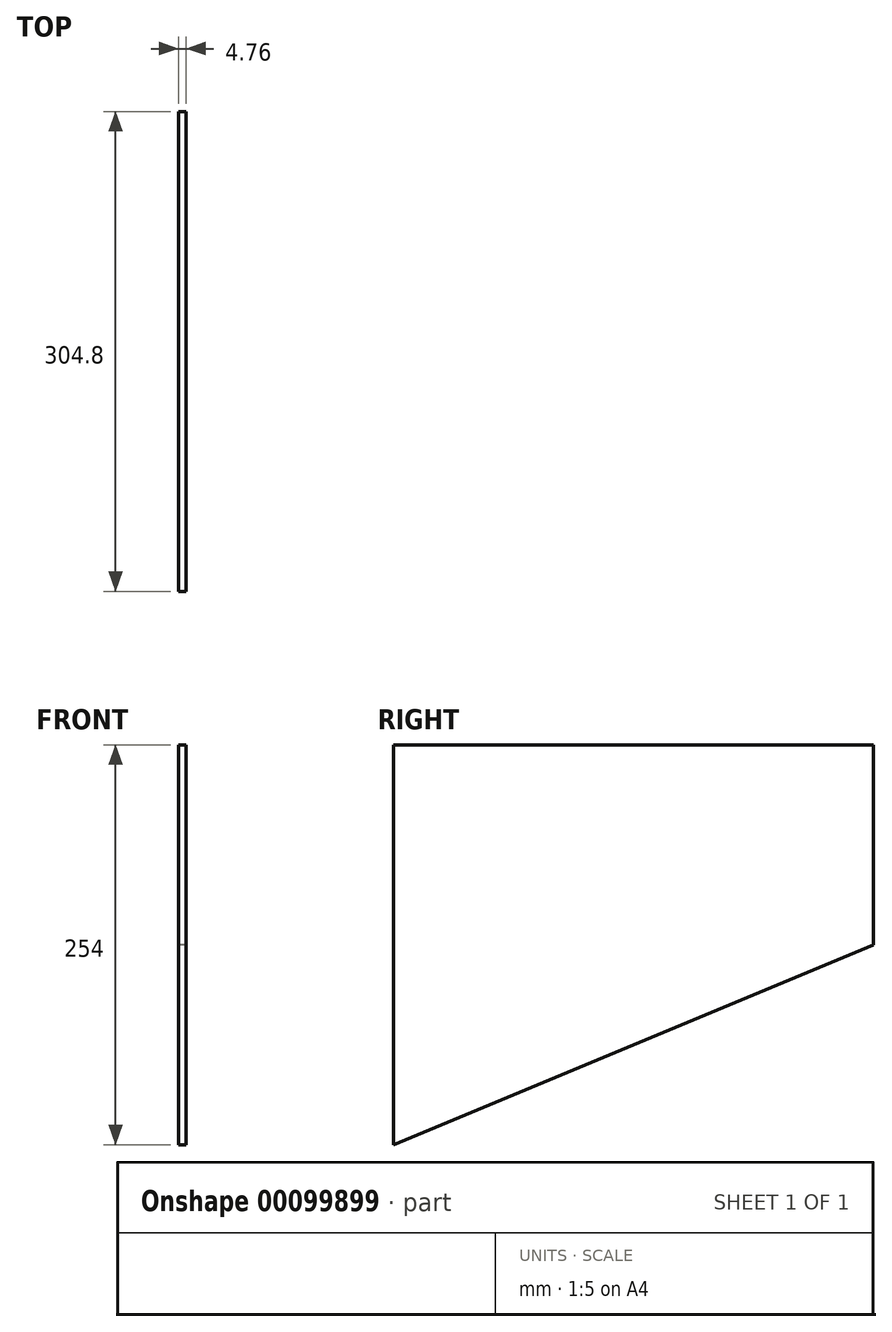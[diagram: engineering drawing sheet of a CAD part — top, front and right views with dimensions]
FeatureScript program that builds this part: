
annotation { "Feature Type Name" : "Feature", "Feature Type Description" : "" }
export const myFeature = defineFeature(function(context is Context, id is Id, definition is map)
    precondition{}
    {
        {
            var Q0;
            Q0=qCreatedBy(makeId("Right.planeOp"),FACE);
            var sketch = newSketch(context, id + "F0", { "sketchPlane" : qUnion([Q0])});
            skLineSegment(sketch, "E0", {"start": v(304.8, 19.22) * mm, "end": v(304.8, -107.78) * mm});
            skLineSegment(sketch, "E1", {"start": v(304.8, -107.78) * mm, "end": v(0, -234.78) * mm});
            skLineSegment(sketch, "E2", {"start": v(0, -234.78) * mm, "end": v(0, 19.22) * mm});
            skLineSegment(sketch, "E3", {"start": v(0, 19.22) * mm, "end": v(304.8, 19.22) * mm});
            skLineSegment(sketch, "E4", {"start": v(304.8, 19.22) * mm, "end": v(304.8, 19.22) * mm});
            skSolve(sketch);
        }
        {
            var Q0;
            Q0 = qSketchRegion(id + "F0", true);
            extrude(context, id + "F1", {"entities" : qUnion([Q0]), "depth" : 4.76 * mm});
        }
    });
